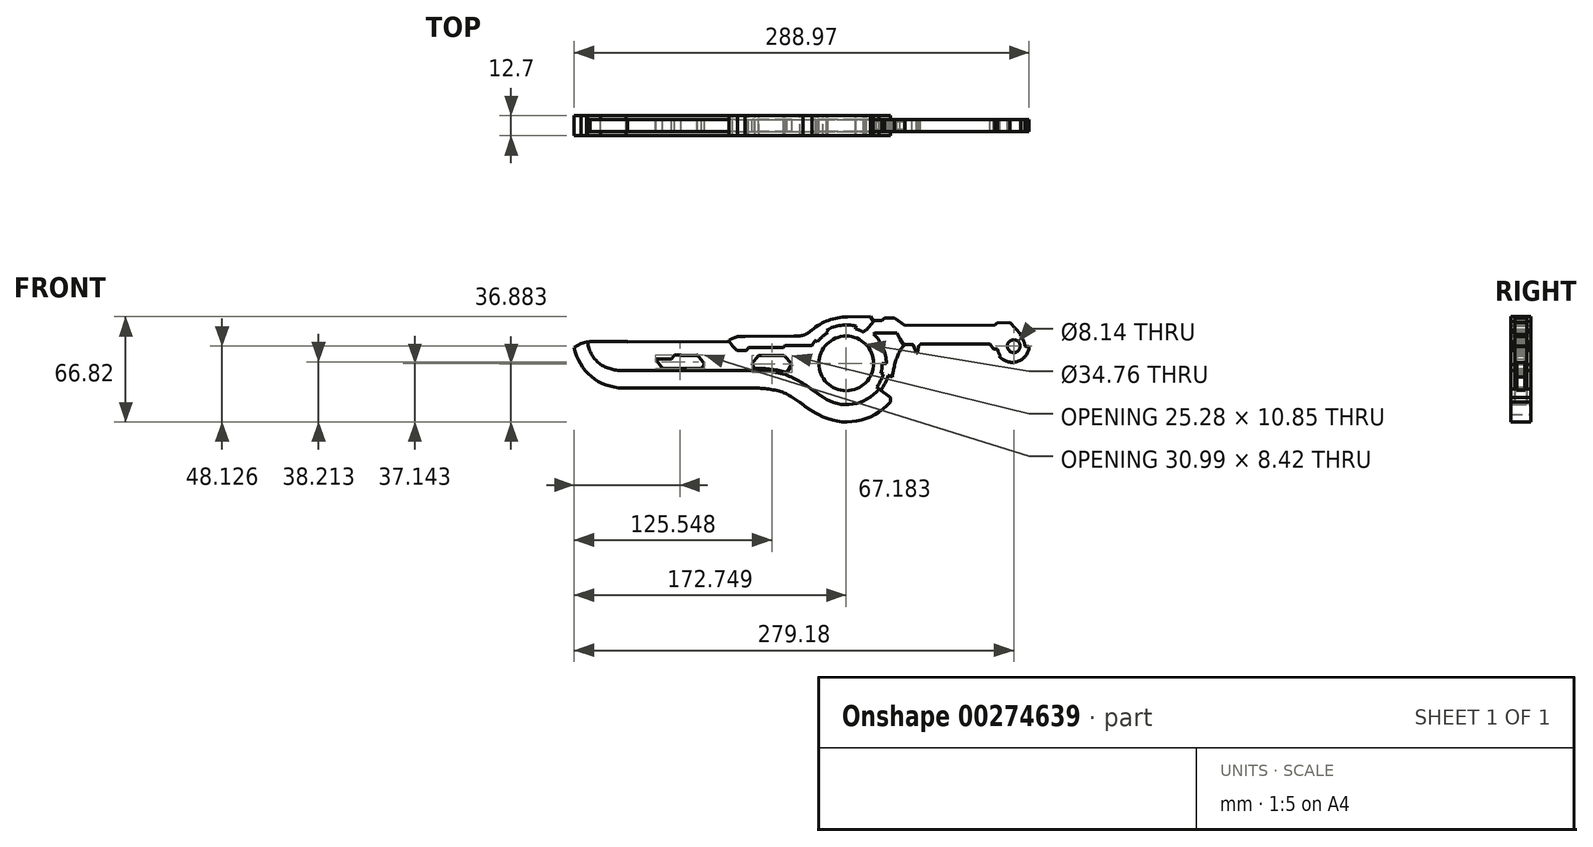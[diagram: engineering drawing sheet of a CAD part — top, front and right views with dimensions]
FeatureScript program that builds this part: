
annotation { "Feature Type Name" : "Feature", "Feature Type Description" : "" }
export const myFeature = defineFeature(function(context is Context, id is Id, definition is map)
    precondition{}
    {
        {
            var Q0;
            Q0=qCreatedBy(makeId("Front.planeOp"),FACE);
            var sketch = newSketch(context, id + "F0", { "sketchPlane" : qUnion([Q0])});
            skCircle(sketch, "E0", {"center": v(29.24, 8.65) * mm, "radius": 17.38 * mm});
            skPoint(sketch, "E0.first.point", {"position": v(17.83, 21.76) * mm});
            skPoint(sketch, "E0.second.point", {"position": v(41.27, 21.2) * mm});
            skPoint(sketch, "E0.third.point", {"position": v(29.08, -8.73) * mm});
            skCircle(sketch, "E1", {"center": v(29.24, 8.65) * mm, "radius": 20.7 * mm});
            skCircle(sketch, "E2", {"center": v(29.24, 8.65) * mm, "radius": 21.47 * mm});
            skCircle(sketch, "E3", {"center": v(29.24, 8.65) * mm, "radius": 22.13 * mm});
            skCircle(sketch, "E4", {"center": v(29.24, 8.65) * mm, "radius": 22.63 * mm});
            skCircle(sketch, "E5", {"center": v(29.24, 8.65) * mm, "radius": 24.48 * mm});
            skPoint(sketch, "E6.first.point", {"position": v(-143.5, 18.88) * mm});
            skPoint(sketch, "E6.second.point", {"position": v(-110.48, -6.87) * mm});
            skPoint(sketch, "E6.third.point", {"position": v(-96.52, 52) * mm});
            skLineSegment(sketch, "E7", {"start": v(-26, -7.07) * mm, "end": v(-112.48, -6.93) * mm});
            skArc(sketch, "E8", {"start": v(11.48, -23.8) * mm, "mid": v(35.86, -27.94) * mm, "end": v(57.4, -15.82) * mm});
            skLineSegment(sketch, "E9", {"start": v(57.4, -15.82) * mm, "end": v(57.4, -13.12) * mm});
            skLineSegment(sketch, "E10", {"start": v(57.4, -13.12) * mm, "end": v(48.62, -6.3) * mm});
            skCircle(sketch, "E11", {"center": v(29.24, 8.65) * mm, "radius": 27.75 * mm});
            skFitSpline(sketch, "E12", {"points": [v(-26, -7.07) * mm, v(-11.6, -9.48) * mm, v(0, -16.22) * mm], "startDerivative": vector(29.36, -2.4) * mm, "endDerivative": vector(22.6, -16) * mm});
            skFitSpline(sketch, "E13", {"points": [v(0, -16.22) * mm, v(4.95, -19.83) * mm, v(11.48, -23.8) * mm], "startDerivative": vector(10.02, -7.68) * mm, "endDerivative": vector(12.9, -7.5) * mm});
            skLineSegment(sketch, "E14", {"start": v(-45.35, 22.68) * mm, "end": v(-109.68, 22.35) * mm});
            skLineSegment(sketch, "E15", {"start": v(-109.68, 22.35) * mm, "end": v(-109.77, 22.57) * mm});
            skLineSegment(sketch, "E16", {"start": v(-109.77, 22.57) * mm, "end": v(-133.52, 22.52) * mm});
            skLineSegment(sketch, "E17", {"start": v(-133.52, 22.52) * mm, "end": v(-134.34, 22.18) * mm});
            skLineSegment(sketch, "E18", {"start": v(-134.34, 22.18) * mm, "end": v(-135.72, 22.18) * mm});
            skLineSegment(sketch, "E19", {"start": v(-135.72, 22.18) * mm, "end": v(-139.29, 21.33) * mm});
            skLineSegment(sketch, "E20", {"start": v(-139.29, 21.33) * mm, "end": v(-143.5, 18.88) * mm});
            skLineSegment(sketch, "E21", {"start": v(-91.64, 11.63) * mm, "end": v(-81.75, 11.63) * mm});
            skLineSegment(sketch, "E22", {"start": v(-81.75, 11.63) * mm, "end": v(-79.7, 13.93) * mm});
            skLineSegment(sketch, "E23", {"start": v(-79.7, 13.93) * mm, "end": v(-75.8, 13.93) * mm});
            skLineSegment(sketch, "E24", {"start": v(-75.8, 13.93) * mm, "end": v(-75.69, 13.76) * mm});
            skLineSegment(sketch, "E25", {"start": v(-75.69, 13.76) * mm, "end": v(-65.6, 13.76) * mm});
            skLineSegment(sketch, "E26", {"start": v(-65.6, 13.76) * mm, "end": v(-65.48, 13.93) * mm});
            skLineSegment(sketch, "E27", {"start": v(-65.48, 13.93) * mm, "end": v(-65.22, 13.93) * mm});
            skLineSegment(sketch, "E28", {"start": v(-65.22, 13.93) * mm, "end": v(-60.83, 8.35) * mm});
            skLineSegment(sketch, "E29", {"start": v(-60.83, 8.35) * mm, "end": v(-62.76, 5.51) * mm});
            skLineSegment(sketch, "E30", {"start": v(-62.76, 5.51) * mm, "end": v(-87.29, 5.51) * mm});
            skLineSegment(sketch, "E31", {"start": v(-91.82, 11.4) * mm, "end": v(-91.64, 11.63) * mm});
            skLineSegment(sketch, "E32", {"start": v(-91.82, 11.4) * mm, "end": v(-87.45, 5.51) * mm});
            skLineSegment(sketch, "E33", {"start": v(-87.45, 5.51) * mm, "end": v(-87.29, 5.51) * mm});
            skFitSpline(sketch, "E34", {"points": [v(65.9, 19.93) * mm, v(64.82, 18.86) * mm, v(63.57, 16.98) * mm, v(62.1, 14.02) * mm, v(60.68, 10.24) * mm, v(59.68, 6.44) * mm, v(59.05, 3.53) * mm, v(58.8, 2.11) * mm, v(58.64, 0.2) * mm], "startDerivative": vector(-24.31, -21.02) * mm, "endDerivative": vector(1.06, -18.55) * mm});
            skLineSegment(sketch, "E35", {"start": v(58.64, 0.2) * mm, "end": v(56.12, 0.94) * mm});
            skLineSegment(sketch, "E36", {"start": v(56.12, 0.94) * mm, "end": v(55.77, 0.83) * mm});
            skLineSegment(sketch, "E37", {"start": v(55.77, 0.83) * mm, "end": v(51.32, 2.65) * mm});
            skLineSegment(sketch, "E38", {"start": v(-45.26, 23.5) * mm, "end": v(-45.14, 22.85) * mm});
            skLineSegment(sketch, "E39", {"start": v(-45.14, 22.85) * mm, "end": v(-45.35, 22.68) * mm});
            skPoint(sketch, "E40", {"position": v(-39.93, 25.63) * mm});
            skArc(sketch, "E41", {"start": v(-39.93, 25.63) * mm, "mid": v(-42.62, 24.64) * mm, "end": v(-45.26, 23.5) * mm});
            skLineSegment(sketch, "E42", {"start": v(44.68, 38.33) * mm, "end": v(29.93, 38.2) * mm});
            skLineSegment(sketch, "E43", {"start": v(46.56, 35.29) * mm, "end": v(44.68, 38.33) * mm});
            skLineSegment(sketch, "E44", {"start": v(41.99, 29.9) * mm, "end": v(46.56, 35.29) * mm});
            skLineSegment(sketch, "E45", {"start": v(41.99, 29.9) * mm, "end": v(41.5, 29.93) * mm});
            skLineSegment(sketch, "E46", {"start": v(41.5, 29.93) * mm, "end": v(40.3, 28.52) * mm});
            skLineSegment(sketch, "E47", {"start": v(35.06, 30.67) * mm, "end": v(35.48, 32.32) * mm});
            skArc(sketch, "E48", {"start": v(40.3, 28.52) * mm, "mid": v(37.75, 29.76) * mm, "end": v(35.06, 30.67) * mm});
            skLineSegment(sketch, "E49", {"start": v(16.78, 29.72) * mm, "end": v(17.65, 28.27) * mm});
            skLineSegment(sketch, "E50", {"start": v(9.66, 23.35) * mm, "end": v(10.94, 22.33) * mm});
            skArc(sketch, "E51", {"start": v(17.65, 28.27) * mm, "mid": v(14.03, 25.6) * mm, "end": v(10.94, 22.33) * mm});
            skLineSegment(sketch, "E52", {"start": v(-9.71, 20.17) * mm, "end": v(7.64, 20.17) * mm});
            skLineSegment(sketch, "E53", {"start": v(-32.68, 18.68) * mm, "end": v(-10.61, 18.68) * mm});
            skLineSegment(sketch, "E54", {"start": v(-10.61, 18.68) * mm, "end": v(-9.71, 20.17) * mm});
            skLineSegment(sketch, "E55", {"start": v(-34.05, 16.76) * mm, "end": v(-32.68, 18.68) * mm});
            skLineSegment(sketch, "E56", {"start": v(-40.15, 16.76) * mm, "end": v(-34.05, 16.76) * mm});
            skLineSegment(sketch, "E57", {"start": v(-40.15, 16.76) * mm, "end": v(-42.92, 19.7) * mm});
            skLineSegment(sketch, "E58", {"start": v(-42.92, 19.7) * mm, "end": v(-45.14, 22.85) * mm});
            skArc(sketch, "E59", {"start": v(29.93, 38.2) * mm, "mid": v(17.99, 36.03) * mm, "end": v(7.45, 30.01) * mm});
            skArc(sketch, "E60", {"start": v(1.88, 26.48) * mm, "mid": v(4.84, 27.97) * mm, "end": v(7.45, 30.01) * mm});
            skArc(sketch, "E61", {"start": v(-3.85, 25.98) * mm, "mid": v(-0.98, 26.1) * mm, "end": v(1.88, 26.48) * mm});
            skLineSegment(sketch, "E62", {"start": v(-3.85, 25.98) * mm, "end": v(-35.06, 25.8) * mm});
            skLineSegment(sketch, "E63", {"start": v(-35.06, 25.8) * mm, "end": v(-39.93, 25.63) * mm});
            skCircle(sketch, "E64", {"center": v(134.04, 19.12) * mm, "radius": 8.76 * mm});
            skPoint(sketch, "E64.first.point", {"position": v(142.78, 19.68) * mm});
            skPoint(sketch, "E64.second.point", {"position": v(139.83, 25.7) * mm});
            skPoint(sketch, "E64.third.point", {"position": v(126.25, 15.1) * mm});
            skCircle(sketch, "E65", {"center": v(135.67, 19.64) * mm, "radius": 4.07 * mm});
            skPoint(sketch, "E65.first.point", {"position": v(135.84, 23.7) * mm});
            skPoint(sketch, "E65.second.point", {"position": v(139.72, 19.2) * mm});
            skPoint(sketch, "E65.third.point", {"position": v(132.75, 16.8) * mm});
            skCircle(sketch, "E66", {"center": v(134.7, 20.1) * mm, "radius": 10.77 * mm});
            skPoint(sketch, "E66.first.point", {"position": v(126.26, 13.4) * mm});
            skPoint(sketch, "E66.second.point", {"position": v(145.46, 19.41) * mm});
            skPoint(sketch, "E66.third.point", {"position": v(138.7, 10.1) * mm});
            skLineSegment(sketch, "E67", {"start": v(145.46, 19.41) * mm, "end": v(143.11, 19.41) * mm});
            skLineSegment(sketch, "E68", {"start": v(143.11, 19.41) * mm, "end": v(142.78, 19.68) * mm});
            skCircle(sketch, "E69", {"center": v(135.8, 19.46) * mm, "radius": 6.56 * mm});
            skPoint(sketch, "E69.first.point", {"position": v(133.63, 25.65) * mm});
            skPoint(sketch, "E69.second.point", {"position": v(142.36, 19.47) * mm});
            skPoint(sketch, "E69.third.point", {"position": v(130.34, 15.81) * mm});
            skLineSegment(sketch, "E70", {"start": v(130.34, 15.81) * mm, "end": v(126.26, 13.4) * mm});
            skLineSegment(sketch, "E71", {"start": v(129.24, 19.5) * mm, "end": v(126.26, 19.5) * mm});
            skLineSegment(sketch, "E72", {"start": v(126.26, 19.5) * mm, "end": v(125.35, 17.97) * mm});
            skLineSegment(sketch, "E73", {"start": v(125.35, 17.97) * mm, "end": v(122.77, 17.97) * mm});
            skLineSegment(sketch, "E74", {"start": v(122.77, 17.97) * mm, "end": v(120.41, 20.87) * mm});
            skLineSegment(sketch, "E75", {"start": v(120.41, 20.87) * mm, "end": v(76.37, 20.87) * mm});
            skLineSegment(sketch, "E76", {"start": v(73.73, 15.4) * mm, "end": v(74.55, 15.4) * mm});
            skLineSegment(sketch, "E77", {"start": v(66.83, 20.82) * mm, "end": v(70.9, 20.82) * mm});
            skLineSegment(sketch, "E78", {"start": v(73.73, 15.4) * mm, "end": v(72.1, 20) * mm});
            skArc(sketch, "E79", {"start": v(72.1, 20) * mm, "mid": v(71.64, 20.6) * mm, "end": v(70.9, 20.82) * mm});
            skArc(sketch, "E80", {"start": v(66.83, 20.82) * mm, "mid": v(66.18, 20.56) * mm, "end": v(65.9, 19.93) * mm});
            skLineSegment(sketch, "E81", {"start": v(74.55, 15.4) * mm, "end": v(75.1, 19.25) * mm});
            skArc(sketch, "E82", {"start": v(76.37, 20.87) * mm, "mid": v(75.66, 20.12) * mm, "end": v(75.1, 19.25) * mm});
            skLineSegment(sketch, "E83", {"start": v(46.22, 35.83) * mm, "end": v(52.03, 35.83) * mm, "construction": true});
            skLineSegment(sketch, "E84", {"start": v(52.03, 35.83) * mm, "end": v(53.43, 37.48) * mm, "construction": true});
            skLineSegment(sketch, "E85", {"start": v(53.43, 37.48) * mm, "end": v(59.95, 37.48) * mm, "construction": true});
            skLineSegment(sketch, "E86", {"start": v(59.95, 37.48) * mm, "end": v(53.43, 37.48) * mm});
            skLineSegment(sketch, "E87", {"start": v(52.03, 35.83) * mm, "end": v(53.43, 37.48) * mm});
            skLineSegment(sketch, "E88", {"start": v(52.03, 35.83) * mm, "end": v(46.22, 35.83) * mm});
            skLineSegment(sketch, "E89", {"start": v(59.95, 37.48) * mm, "end": v(66.63, 32.75) * mm});
            skLineSegment(sketch, "E90", {"start": v(66.63, 32.75) * mm, "end": v(123.6, 33.06) * mm});
            skLineSegment(sketch, "E91", {"start": v(123.6, 33.06) * mm, "end": v(125.11, 34.3) * mm});
            skLineSegment(sketch, "E92", {"start": v(125.11, 34.3) * mm, "end": v(125.4, 34.48) * mm});
            skLineSegment(sketch, "E93", {"start": v(125.4, 34.48) * mm, "end": v(133.36, 34.53) * mm});
            skLineSegment(sketch, "E94", {"start": v(133.36, 34.53) * mm, "end": v(140.3, 27.11) * mm});
            skLineSegment(sketch, "E95", {"start": v(140.3, 27.11) * mm, "end": v(139.83, 25.7) * mm});
            skArc(sketch, "E96.trimOffspring", {"start": v(-143.5, 18.88) * mm, "mid": v(-131.87, -0.25) * mm, "end": v(-110.48, -6.87) * mm});
            skLineSegment(sketch, "E97", {"start": v(-30.6, 8.5) * mm, "end": v(-26.36, 13.73) * mm});
            skLineSegment(sketch, "E98", {"start": v(-26.36, 13.73) * mm, "end": v(-10.4, 13.82) * mm});
            skLineSegment(sketch, "E99", {"start": v(-10.4, 13.82) * mm, "end": v(-5.53, 8.57) * mm});
            skLineSegment(sketch, "E100", {"start": v(-5.53, 8.57) * mm, "end": v(-5.32, 8.35) * mm});
            skLineSegment(sketch, "E101", {"start": v(-5.32, 8.35) * mm, "end": v(-8.33, 2.97) * mm});
            skLineSegment(sketch, "E102", {"start": v(-28.95, 5.53) * mm, "end": v(-30.6, 8.5) * mm});
            skArc(sketch, "E103", {"start": v(-8.33, 2.97) * mm, "mid": v(-18.56, 4.93) * mm, "end": v(-28.95, 5.53) * mm});
            skArc(sketch, "E104", {"start": v(-135.03, 22.18) * mm, "mid": v(-132.3, 14.18) * mm, "end": v(-126.63, 7.9) * mm});
            skArc(sketch, "E105", {"start": v(-126.63, 7.9) * mm, "mid": v(-118.85, 4.77) * mm, "end": v(-110.48, 4.2) * mm});
            skLineSegment(sketch, "E106", {"start": v(-110.48, 4.2) * mm, "end": v(-28.8, 4.2) * mm});
            skCircle(sketch, "E107", {"center": v(29.5, 8.53) * mm, "radius": 26.07 * mm});
            skFitSpline(sketch, "E108", {"points": [v(-28.8, 4.2) * mm, v(-5.65, 0) * mm, v(6.44, -7.17) * mm, v(14.5, -12.78) * mm, v(14.52, -12.8) * mm], "startDerivative": vector(87.14, -2.39) * mm, "endDerivative": vector(0.8, -0.7) * mm});
            skLineSegment(sketch, "E109", {"start": v(52.11, 8.6) * mm, "end": v(54.75, 8.6) * mm});
            skArc(sketch, "E110", {"start": v(51.32, 2.65) * mm, "mid": v(51.93, 5.6) * mm, "end": v(52.11, 8.6) * mm});
            skLineSegment(sketch, "E111", {"start": v(46.67, 27.4) * mm, "end": v(47.34, 27.97) * mm});
            skLineSegment(sketch, "E112", {"start": v(47.34, 27.97) * mm, "end": v(61.5, 27.97) * mm});
            skLineSegment(sketch, "E113", {"start": v(61.5, 27.97) * mm, "end": v(63.51, 24.18) * mm});
            skLineSegment(sketch, "E114", {"start": v(63.51, 24.18) * mm, "end": v(65.9, 19.93) * mm});
            skArc(sketch, "E115", {"start": v(54.75, 8.6) * mm, "mid": v(52.6, 18.8) * mm, "end": v(46.67, 27.4) * mm});
            skSolve(sketch);
        }
        {
            var Q0;
            Q0=makeQuery(id+"F0.imprint","IMPRINT",FACE,{"disambiguationData":[TD([[makeQuery(id+"F0.imprint","IMPRINT",EDGE,{"derivedFrom":sQuery(id+"F0.wireOp",EDGE,"E14")}),1.0]])]});
            var Q1;
            {var subQ0=sQuery(id+"F0.wireOp",EDGE,"E52");var subQ1=sQuery(id+"F0.wireOp",EDGE,"E11");var subQ2=makeQuery(id+"F0.imprint","INTERSECT",VERTEX,{"derivedFrom":[subQ1,subQ0]});Q1=makeQuery(id+"F0.imprint","IMPRINT",FACE,{"disambiguationData":[TD([[makeQuery(id+"F0.imprint","IMPRINT",EDGE,{"disambiguationData":[TD([[subQ2,-1.0]])],"derivedFrom":subQ1}),1.0]])]});}
            var Q2;
            {var subQ6=sQuery(id+"F0.wireOp",EDGE,"E5");var subQ8=sQuery(id+"F0.wireOp",EDGE,"E10");var subQ9=makeQuery(id+"F0.imprint","INTERSECT",VERTEX,{"derivedFrom":[subQ6,subQ8]});Q2=makeQuery(id+"F0.imprint","IMPRINT",FACE,{"disambiguationData":[TD([[makeQuery(id+"F0.imprint","IMPRINT",EDGE,{"disambiguationData":[TD([[subQ9,1.0]])],"derivedFrom":subQ6}),-1.0]])]});}
            var Q3;
            Q3=makeQuery(id+"F0.imprint","IMPRINT",FACE,{"disambiguationData":[TD([[makeQuery(id+"F0.imprint","IMPRINT",EDGE,{"derivedFrom":sQuery(id+"F0.wireOp",EDGE,"E4")}),-1.0]])]});
            var Q4;
            Q4=makeQuery(id+"F0.imprint","IMPRINT",FACE,{"disambiguationData":[TD([[makeQuery(id+"F0.imprint","IMPRINT",EDGE,{"derivedFrom":sQuery(id+"F0.wireOp",EDGE,"E3")}),-1.0]])]});
            var Q5;
            Q5=makeQuery(id+"F0.imprint","IMPRINT",FACE,{"disambiguationData":[TD([[makeQuery(id+"F0.imprint","IMPRINT",EDGE,{"derivedFrom":sQuery(id+"F0.wireOp",EDGE,"E2")}),-1.0]])]});
            var Q6;
            Q6=makeQuery(id+"F0.imprint","IMPRINT",FACE,{"disambiguationData":[TD([[makeQuery(id+"F0.imprint","IMPRINT",EDGE,{"derivedFrom":sQuery(id+"F0.wireOp",EDGE,"E1")}),-1.0]])]});
            var Q7;
            Q7=makeQuery(id+"F0.imprint","IMPRINT",FACE,{"disambiguationData":[TD([[makeQuery(id+"F0.imprint","IMPRINT",EDGE,{"derivedFrom":sQuery(id+"F0.wireOp",EDGE,"E0")}),-1.0]])]});
            var Q8;
            {var subQ1=sQuery(id+"F0.wireOp",EDGE,"E45");Q8=makeQuery(id+"F0.imprint","IMPRINT",FACE,{"disambiguationData":[TD([[makeQuery(id+"F0.imprint","IMPRINT",EDGE,{"derivedFrom":subQ1}),1.0]])]});}
            var Q9;
            {var subQ1=sQuery(id+"F0.wireOp",EDGE,"E44");var subQ5=sQuery(id+"F0.wireOp",EDGE,"E11");var subQ6=makeQuery(id+"F0.imprint","INTERSECT",VERTEX,{"derivedFrom":[subQ5,subQ1]});Q9=makeQuery(id+"F0.imprint","IMPRINT",FACE,{"disambiguationData":[TD([[makeQuery(id+"F0.imprint","IMPRINT",EDGE,{"disambiguationData":[TD([[subQ6,1.0]])],"derivedFrom":subQ5}),1.0]])]});}
            var Q10;
            {var subQ1=sQuery(id+"F0.wireOp",EDGE,"E74");Q10=makeQuery(id+"F0.imprint","IMPRINT",FACE,{"disambiguationData":[TD([[makeQuery(id+"F0.imprint","IMPRINT",EDGE,{"derivedFrom":subQ1}),-1.0]])]});}
            var Q11;
            {var subQ0=sQuery(id+"F0.wireOp",EDGE,"E95");Q11=makeQuery(id+"F0.imprint","IMPRINT",FACE,{"disambiguationData":[TD([[makeQuery(id+"F0.imprint","IMPRINT",EDGE,{"derivedFrom":subQ0}),-1.0]])]});}
            var Q12;
            {var subQ8=sQuery(id+"F0.wireOp",EDGE,"E71");Q12=makeQuery(id+"F0.imprint","IMPRINT",FACE,{"disambiguationData":[TD([[makeQuery(id+"F0.imprint","IMPRINT",EDGE,{"derivedFrom":subQ8}),-1.0]])]});}
            var Q13;
            {var subQ0=sQuery(id+"F0.wireOp",EDGE,"E71");Q13=makeQuery(id+"F0.imprint","IMPRINT",FACE,{"disambiguationData":[TD([[makeQuery(id+"F0.imprint","IMPRINT",EDGE,{"derivedFrom":subQ0}),1.0]])]});}
            var Q14;
            {var subQ1=sQuery(id+"F0.wireOp",EDGE,"E67");Q14=makeQuery(id+"F0.imprint","IMPRINT",FACE,{"disambiguationData":[TD([[makeQuery(id+"F0.imprint","IMPRINT",EDGE,{"derivedFrom":subQ1}),1.0]])]});}
            var Q15;
            Q15=makeQuery(id+"F0.imprint","IMPRINT",FACE,{"disambiguationData":[TD([[makeQuery(id+"F0.imprint","IMPRINT",EDGE,{"derivedFrom":sQuery(id+"F0.wireOp",EDGE,"E65")}),-1.0]])]});
            extrude(context, id + "F1", {"entities" : qUnion([Q0, Q1, Q2, Q3, Q4, Q5, Q6, Q7, Q8, Q9, Q10, Q11, Q12, Q13, Q14, Q15]), "endBound" : BoundingType.SYMMETRIC, "depth" : 7.62 * mm});
        }
        {
            var Q0;
            Q0=makeQuery(id+"F0.imprint","IMPRINT",FACE,{"disambiguationData":[TD([[makeQuery(id+"F0.imprint","IMPRINT",EDGE,{"derivedFrom":sQuery(id+"F0.wireOp",EDGE,"E38")}),1.0]])]});
            var Q1;
            {var subQ0=sQuery(id+"F0.wireOp",EDGE,"E44");var subQ1=sQuery(id+"F0.wireOp",EDGE,"E11");var subQ2=makeQuery(id+"F0.imprint","INTERSECT",VERTEX,{"derivedFrom":[subQ1,subQ0]});Q1=makeQuery(id+"F0.imprint","IMPRINT",FACE,{"disambiguationData":[TD([[makeQuery(id+"F0.imprint","IMPRINT",EDGE,{"disambiguationData":[TD([[subQ2,-1.0]])],"derivedFrom":subQ1}),1.0]])]});}
            var Q2;
            {var subQ8=sQuery(id+"F0.wireOp",EDGE,"E45");Q2=makeQuery(id+"F0.imprint","IMPRINT",FACE,{"disambiguationData":[TD([[makeQuery(id+"F0.imprint","IMPRINT",EDGE,{"derivedFrom":subQ8}),-1.0]])]});}
            var Q3;
            {var subQ0=sQuery(id+"F0.wireOp",EDGE,"E49");Q3=makeQuery(id+"F0.imprint","IMPRINT",FACE,{"disambiguationData":[TD([[makeQuery(id+"F0.imprint","IMPRINT",EDGE,{"derivedFrom":subQ0}),-1.0]])]});}
            var Q4;
            {var subQ0=sQuery(id+"F0.wireOp",EDGE,"E47");Q4=makeQuery(id+"F0.imprint","IMPRINT",FACE,{"disambiguationData":[TD([[makeQuery(id+"F0.imprint","IMPRINT",EDGE,{"derivedFrom":subQ0}),-1.0]])]});}
            var Q5;
            {var subQ10=sQuery(id+"F0.wireOp",EDGE,"E7");Q5=makeQuery(id+"F0.imprint","IMPRINT",FACE,{"disambiguationData":[TD([[makeQuery(id+"F0.imprint","IMPRINT",EDGE,{"derivedFrom":subQ10}),-1.0]])]});}
            var Q6;
            {var subQ3=sQuery(id+"F0.wireOp",EDGE,"E10");var subQ6=sQuery(id+"F0.wireOp",EDGE,"E11");var subQ7=makeQuery(id+"F0.imprint","INTERSECT",VERTEX,{"derivedFrom":[subQ3,subQ6]});Q6=makeQuery(id+"F0.imprint","IMPRINT",FACE,{"disambiguationData":[TD([[makeQuery(id+"F0.imprint","IMPRINT",EDGE,{"disambiguationData":[TD([[subQ7,-1.0]])],"derivedFrom":subQ3}),1.0]])]});}
            extrude(context, id + "F2", {"entities" : qUnion([Q0, Q1, Q2, Q3, Q4, Q5, Q6]), "endBound" : BoundingType.SYMMETRIC, "depth" : 12.7 * mm});
        }
        {
            var Q0;
            Q0=makeQuery(id+"F0.imprint","IMPRINT",FACE,{"disambiguationData":[TD([[makeQuery(id+"F0.imprint","IMPRINT",EDGE,{"derivedFrom":sQuery(id+"F0.wireOp",EDGE,"E34")}),-1.0]])]});
            var Q1;
            {var subQ1=sQuery(id+"F0.wireOp",EDGE,"E36");var subQ5=sQuery(id+"F0.wireOp",EDGE,"E11");var subQ6=makeQuery(id+"F0.imprint","INTERSECT",VERTEX,{"derivedFrom":[subQ5,subQ1]});Q1=makeQuery(id+"F0.imprint","IMPRINT",FACE,{"disambiguationData":[TD([[makeQuery(id+"F0.imprint","IMPRINT",EDGE,{"disambiguationData":[TD([[subQ6,-1.0]])],"derivedFrom":subQ5}),1.0]])]});}
            var Q2;
            {var subQ0=sQuery(id+"F0.wireOp",EDGE,"E115");Q2=makeQuery(id+"F0.imprint","IMPRINT",FACE,{"disambiguationData":[TD([[makeQuery(id+"F0.imprint","IMPRINT",EDGE,{"derivedFrom":subQ0}),-1.0]])]});}
            var Q3;
            {var subQ5=sQuery(id+"F0.wireOp",EDGE,"E110");Q3=makeQuery(id+"F0.imprint","IMPRINT",FACE,{"disambiguationData":[TD([[makeQuery(id+"F0.imprint","IMPRINT",EDGE,{"derivedFrom":subQ5}),-1.0]])]});}
            var Q4;
            {var subQ5=sQuery(id+"F0.wireOp",EDGE,"E11");var subQ7=sQuery(id+"F0.wireOp",EDGE,"E10");var subQ8=makeQuery(id+"F0.imprint","INTERSECT",VERTEX,{"derivedFrom":[subQ7,subQ5]});Q4=makeQuery(id+"F0.imprint","IMPRINT",FACE,{"disambiguationData":[TD([[makeQuery(id+"F0.imprint","IMPRINT",EDGE,{"disambiguationData":[TD([[subQ8,-1.0]])],"derivedFrom":subQ7}),-1.0]])]});}
            var Q5;
            {var subQ0=sQuery(id+"F0.wireOp",EDGE,"E10");var subQ1=sQuery(id+"F0.wireOp",EDGE,"E5");var subQ2=makeQuery(id+"F0.imprint","INTERSECT",VERTEX,{"derivedFrom":[subQ1,subQ0]});Q5=makeQuery(id+"F0.imprint","IMPRINT",FACE,{"disambiguationData":[TD([[makeQuery(id+"F0.imprint","IMPRINT",EDGE,{"disambiguationData":[TD([[subQ2,-1.0]])],"derivedFrom":subQ1}),-1.0]])]});}
            extrude(context, id + "F3", {"entities" : qUnion([Q0, Q1, Q2, Q3, Q4, Q5]), "endBound" : BoundingType.SYMMETRIC, "depth" : 5.08 * mm});
        }
    });
